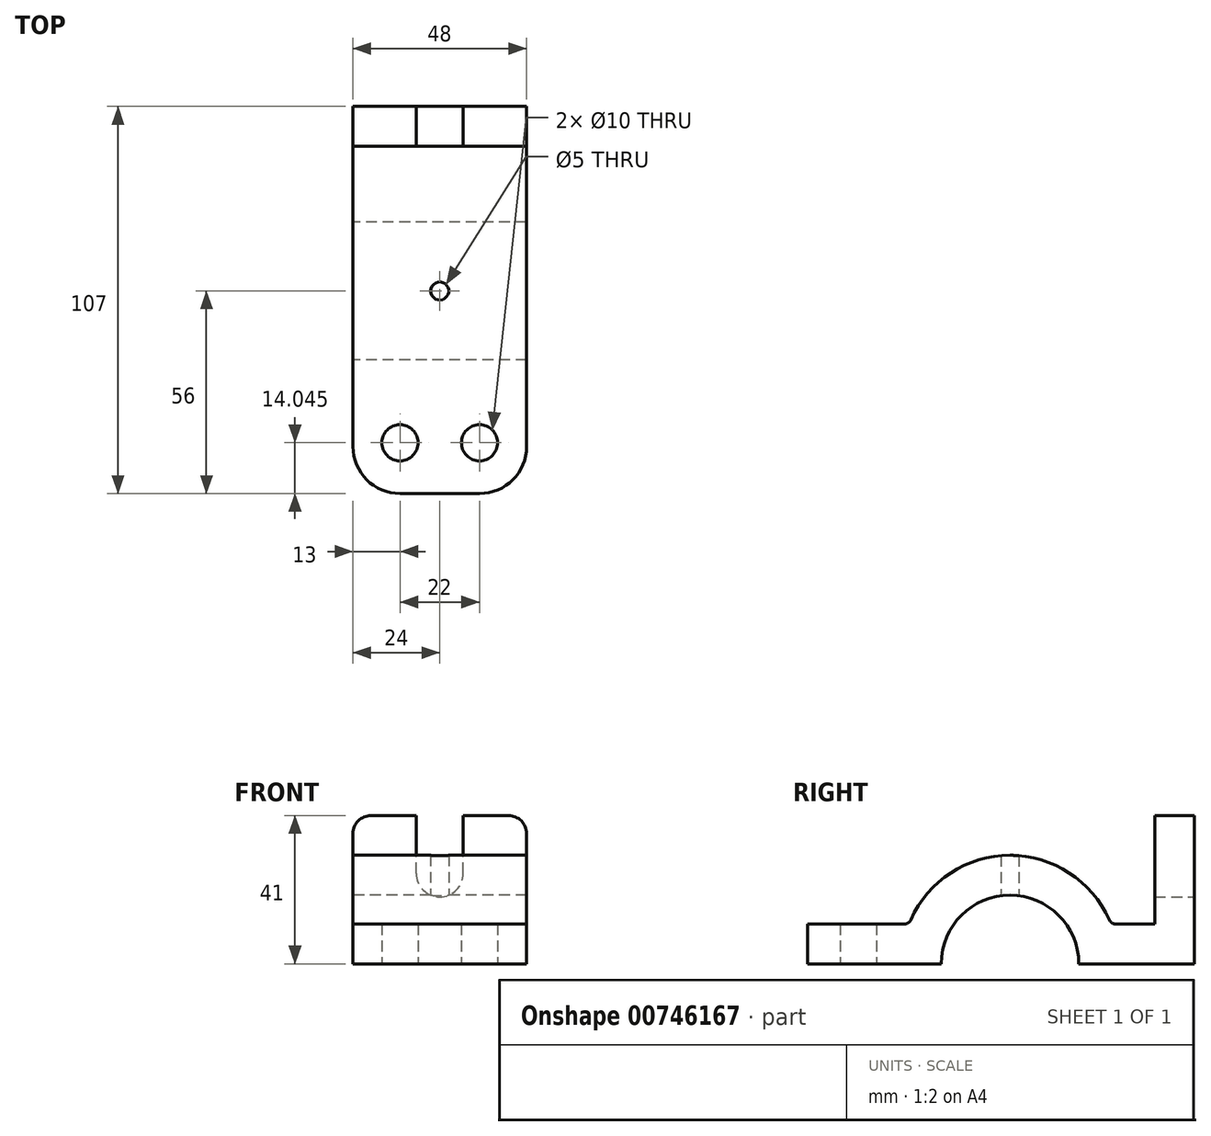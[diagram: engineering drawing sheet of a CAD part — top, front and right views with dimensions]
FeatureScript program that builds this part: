
annotation { "Feature Type Name" : "Feature", "Feature Type Description" : "" }
export const myFeature = defineFeature(function(context is Context, id is Id, definition is map)
    precondition{}
    {
        {
            var Q0;
            Q0=qCreatedBy(makeId("Right.planeOp"),FACE);
            var sketch = newSketch(context, id + "F0", { "sketchPlane" : qUnion([Q0])});
            skCircle(sketch, "E0", {"center": v(0, 0) * mm, "radius": 19 * mm});
            skCircle(sketch, "E1", {"center": v(0, 0) * mm, "radius": 30 * mm});
            skLineSegment(sketch, "E2.bottom", {"start": v(-56, 0) * mm, "end": v(51, 0) * mm});
            skLineSegment(sketch, "E2.top", {"start": v(-56, 11) * mm, "end": v(51, 11) * mm});
            skLineSegment(sketch, "E2.left", {"start": v(-56, 0) * mm, "end": v(-56, 11) * mm});
            skLineSegment(sketch, "E2.right", {"start": v(51, 0) * mm, "end": v(51, 11) * mm});
            skLineSegment(sketch, "E3.bottom", {"start": v(51, 11) * mm, "end": v(40, 11) * mm});
            skLineSegment(sketch, "E3.top", {"start": v(51, 41) * mm, "end": v(40, 41) * mm});
            skLineSegment(sketch, "E3.left", {"start": v(51, 11) * mm, "end": v(51, 41) * mm});
            skLineSegment(sketch, "E3.right", {"start": v(40, 11) * mm, "end": v(40, 41) * mm});
            skSolve(sketch);
        }
        {
            var Q0;
            {var subQ5=sQuery(id+"F0.wireOp",EDGE,"E2.left");Q0=makeQuery(id+"F0.imprint","IMPRINT",FACE,{"disambiguationData":[TD([[makeQuery(id+"F0.imprint","IMPRINT",EDGE,{"derivedFrom":subQ5}),-1.0]])]});}
            var Q1;
            {var subQ0=sQuery(id+"F0.wireOp",EDGE,"E2.bottom");var subQ1=sQuery(id+"F0.wireOp",EDGE,"E0");var subQ2=makeQuery(id+"F0.imprint","INTERSECT",VERTEX,{"disambiguationData":[OD(0.0)],"derivedFrom":[subQ1,subQ0]});Q1=makeQuery(id+"F0.imprint","IMPRINT",FACE,{"disambiguationData":[TD([[makeQuery(id+"F0.imprint","IMPRINT",EDGE,{"disambiguationData":[TD([[subQ2,1.0]])],"derivedFrom":subQ1}),-1.0]])]});}
            var Q2;
            {var subQ0=sQuery(id+"F0.wireOp",EDGE,"E2.top");var subQ1=sQuery(id+"F0.wireOp",EDGE,"E0");var subQ2=makeQuery(id+"F0.imprint","INTERSECT",VERTEX,{"disambiguationData":[OD(0.0)],"derivedFrom":[subQ1,subQ0]});Q2=makeQuery(id+"F0.imprint","IMPRINT",FACE,{"disambiguationData":[TD([[makeQuery(id+"F0.imprint","IMPRINT",EDGE,{"disambiguationData":[TD([[subQ2,1.0]])],"derivedFrom":subQ1}),-1.0]])]});}
            var Q3;
            {var subQ0=sQuery(id+"F0.wireOp",EDGE,"E2.top");var subQ1=sQuery(id+"F0.wireOp",EDGE,"E0");var subQ2=makeQuery(id+"F0.imprint","INTERSECT",VERTEX,{"disambiguationData":[OD(1.0)],"derivedFrom":[subQ1,subQ0]});Q3=makeQuery(id+"F0.imprint","IMPRINT",FACE,{"disambiguationData":[TD([[makeQuery(id+"F0.imprint","IMPRINT",EDGE,{"disambiguationData":[TD([[subQ2,1.0]])],"derivedFrom":subQ1}),-1.0]])]});}
            var Q4;
            {var subQ0=sQuery(id+"F0.wireOp",EDGE,"E2.right");Q4=makeQuery(id+"F0.imprint","IMPRINT",FACE,{"disambiguationData":[TD([[makeQuery(id+"F0.imprint","IMPRINT",EDGE,{"derivedFrom":subQ0}),1.0]])]});}
            var Q5;
            Q5=makeQuery(id+"F0.imprint","IMPRINT",FACE,{"disambiguationData":[TD([[makeQuery(id+"F0.imprint","IMPRINT",EDGE,{"derivedFrom":sQuery(id+"F0.wireOp",EDGE,"E3.top")}),1.0]])]});
            extrude(context, id + "F1", {"entities" : qUnion([Q0, Q1, Q2, Q3, Q4, Q5]), "endBound" : BoundingType.SYMMETRIC, "depth" : 48 * mm});
        }
        {
            var Q0;
            Q0=makeQuery(id+"F1.opExtrude","SWEPT_FACE",FACE,{"disambiguationData":[OSD([sQuery(id+"F0.wireOp",EDGE,"E2.right"),sQuery(id+"F0.wireOp",EDGE,"E3.left")])]});
            var sketch = newSketch(context, id + "F2", { "sketchPlane" : qUnion([Q0])});
            skLineSegment(sketch, "E4", {"start": v(0, 0) * mm, "end": v(0, 41) * mm, "construction": true});
            skCircle(sketch, "E5", {"center": v(0, 25) * mm, "radius": 6.5 * mm});
            skLineSegment(sketch, "E6", {"start": v(-6.5, 25) * mm, "end": v(-6.5, 41) * mm});
            skLineSegment(sketch, "E7", {"start": v(6.5, 25) * mm, "end": v(6.5, 41) * mm});
            skSolve(sketch);
        }
        {
            var Q0;
            {var subQ0=sQuery(id+"F2.wireOp",EDGE,"E5");var subQ2=makeQuery(id+"F2.imprint","INTERSECT",VERTEX,{"derivedFrom":[subQ0,sQuery(id+"F2.wireOp",EDGE,"E6")]});Q0=makeQuery(id+"F2.imprint","IMPRINT",FACE,{"disambiguationData":[TD([[makeQuery(id+"F2.imprint","IMPRINT",EDGE,{"disambiguationData":[TD([[subQ2,1.0]])],"derivedFrom":subQ0}),1.0]])]});}
            var Q1;
            {var subQ2=sQuery(id+"F2.wireOp",EDGE,"E6");Q1=makeQuery(id+"F2.imprint","IMPRINT",FACE,{"disambiguationData":[TD([[makeQuery(id+"F2.imprint","IMPRINT",EDGE,{"derivedFrom":subQ2}),-1.0]])]});}
            var Q2;
            Q2=makeQuery(id+"F1.opExtrude","SWEPT_FACE",FACE,{"disambiguationData":[OSD([sQuery(id+"F0.wireOp",EDGE,"E3.right")])]});
            extrude(context, id + "F3", {"entities" : qUnion([Q0, Q1]), "operationType" : NewBodyOperationType.REMOVE, "endBound" : BoundingType.UP_TO_SURFACE, "oppositeDirection" : true, "endBoundEntityFace" : qUnion([Q2]), "depth" : 25 * mm});
        }
        {
            var Q0;
            Q0=qCreatedBy(makeId("Top.planeOp"),FACE);
            var sketch = newSketch(context, id + "F4", { "sketchPlane" : qUnion([Q0])});
            skCircle(sketch, "E8", {"center": v(0, 0) * mm, "radius": 2.5 * mm});
            skLineSegment(sketch, "E9", {"start": v(24, -41.96) * mm, "end": v(-24, -41.96) * mm, "construction": true});
            skLineSegment(sketch, "E10", {"start": v(0, -56) * mm, "end": v(0, -27.91) * mm, "construction": true});
            skCircle(sketch, "E11", {"center": v(-11, -41.96) * mm, "radius": 5 * mm});
            skCircle(sketch, "E12", {"center": v(11, -41.96) * mm, "radius": 5 * mm});
            skSolve(sketch);
        }
        {
            var Q0;
            Q0=qSketchRegion(id+"F4",true);
            extrude(context, id + "F5", {"entities" : qUnion([Q0]), "operationType" : NewBodyOperationType.REMOVE, "endBound" : BoundingType.THROUGH_ALL, "depth" : 25 * mm});
        }
        {
            var Q0;
            Q0=makeQuery(id+"F1.opExtrude","CAP_EDGE",EDGE,{"disambiguationData":[OSD([sQuery(id+"F0.wireOp",EDGE,"E2.left")])],"isStart":false});
            var Q1;
            Q1=makeQuery(id+"F1.opExtrude","CAP_EDGE",EDGE,{"disambiguationData":[OSD([sQuery(id+"F0.wireOp",EDGE,"E2.left")])],"isStart":true});
            fillet(context, id + "F6", {"entities" : qUnion([Q0, Q1]), "radius" : 13 * mm, "tangentPropagation" : true, "allowEdgeOverflow" : false});
        }
        {
            var Q0;
            Q0=makeQuery(id+"F1.opExtrude","CAP_EDGE",EDGE,{"disambiguationData":[OSD([sQuery(id+"F0.wireOp",EDGE,"E3.top")])],"isStart":false});
            var Q1;
            Q1=makeQuery(id+"F1.opExtrude","CAP_EDGE",EDGE,{"disambiguationData":[OSD([sQuery(id+"F0.wireOp",EDGE,"E3.top")])],"isStart":true});
            fillet(context, id + "F7", {"entities" : qUnion([Q0, Q1]), "radius" : 5 * mm, "tangentPropagation" : true, "allowEdgeOverflow" : false});
        }
        {
            var Q0;
            {var subQ0=sQuery(id+"F0.wireOp",EDGE,"E2.top");var subQ1=sQuery(id+"F0.wireOp",EDGE,"E1");Q0=makeQuery(id+"F1.opExtrude","SWEPT_EDGE",EDGE,{"disambiguationData":[OSD([subQ1,subQ0]),TDD([makeQuery(id+"F0.imprint","INTERSECT",VERTEX,{"disambiguationData":[OD(1.0)],"derivedFrom":[subQ1,subQ0]})])]});}
            var Q1;
            {var subQ0=sQuery(id+"F0.wireOp",EDGE,"E2.top");var subQ1=sQuery(id+"F0.wireOp",EDGE,"E1");Q1=makeQuery(id+"F1.opExtrude","SWEPT_EDGE",EDGE,{"disambiguationData":[OSD([subQ1,subQ0]),TDD([makeQuery(id+"F0.imprint","INTERSECT",VERTEX,{"disambiguationData":[OD(0.0)],"derivedFrom":[subQ1,subQ0]})])]});}
            fillet(context, id + "F8", {"entities" : qUnion([Q0, Q1]), "radius" : 2 * mm, "tangentPropagation" : true, "allowEdgeOverflow" : false});
        }
    });
